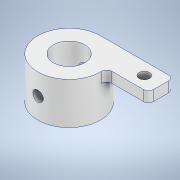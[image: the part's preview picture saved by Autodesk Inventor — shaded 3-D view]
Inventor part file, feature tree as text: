
AUTODESK INVENTOR PART (.ipt)
format: ipt  version: 2022.2 (Build 262287030, 287C)  size: 157,696 bytes
history: native  units: in
note: dims shown in document units (in); Inventor stores cm internally (conversion verified against a paired STEP export)
features: extrude x3, sketch x3, fillet x1
ambient origin geometry x8: Origin, YZ Plane, XZ Plane, XY Plane, X Axis, Y Axis, Z Axis, Center Point
bodies: Solid1 (feature_tree)
feature tree (7):
  extrude  "Extrusion1"  Depth=0.75in
  extrude  "Extrusion2"  Depth=1.75in
  fillet  "Fillet1"  Radius=0.6in
  extrude  "Extrusion3"  Depth=0.125in
  sketch  "Sketch1"  dims[d0=1.5in d1=0.75in]
  sketch  "Sketch2"  dims[d2=1.0in d3=0.0in d4=1.75in d5=0.6in]
  sketch  "Sketch3"  dims[d6=0.25in d7=0.4in d8=0.25in d9=0.0in d10=0.125in d11=0.5in d12=0.25in d13=0.0in d14=0.0in]
